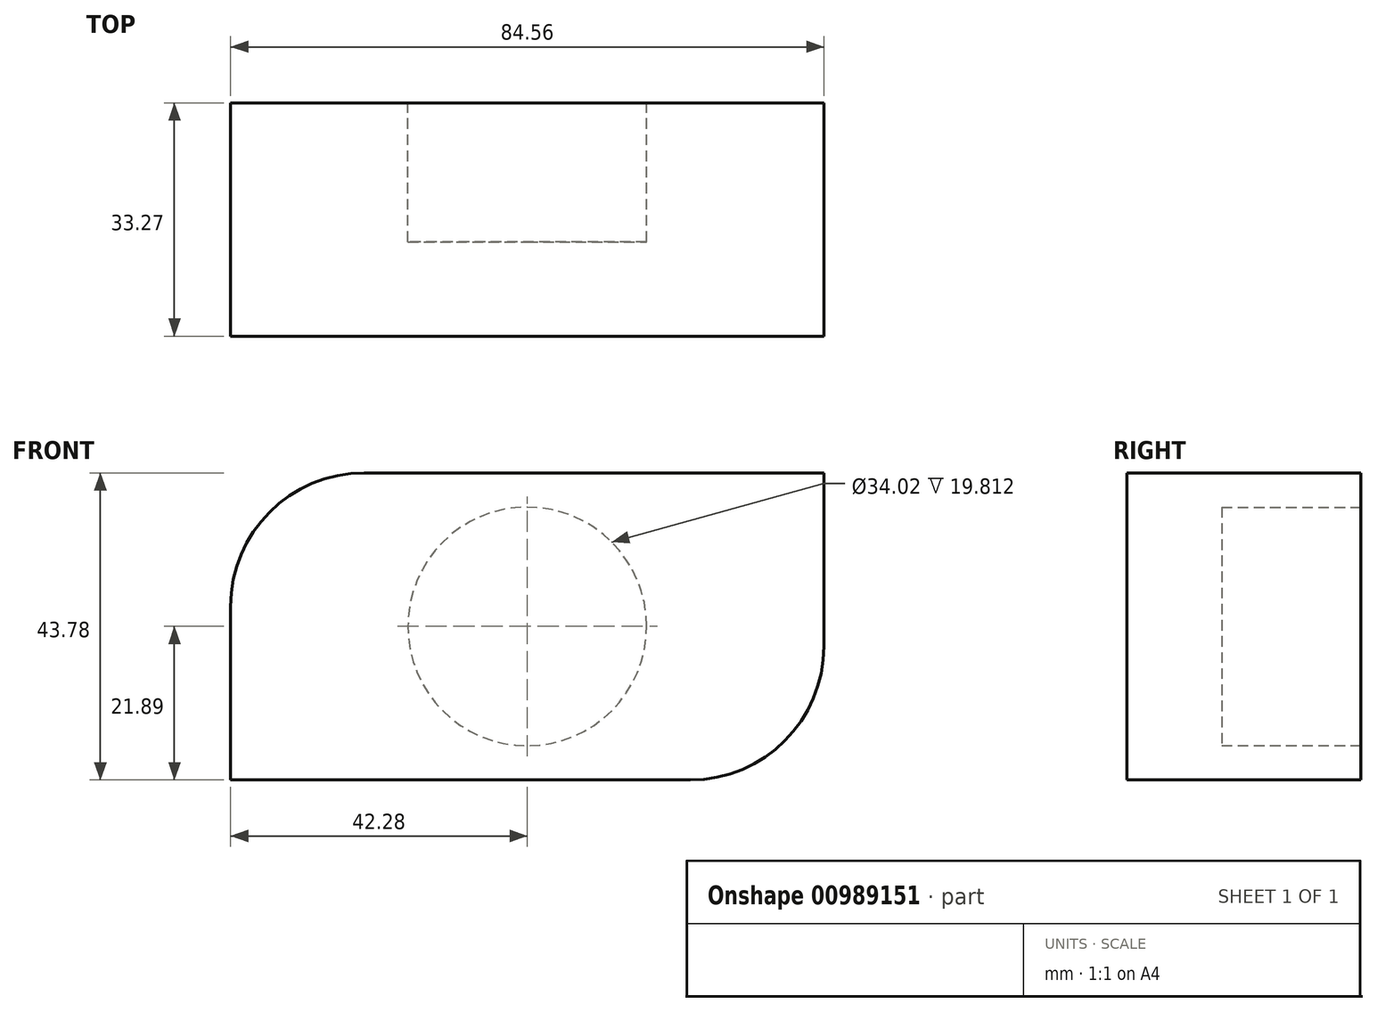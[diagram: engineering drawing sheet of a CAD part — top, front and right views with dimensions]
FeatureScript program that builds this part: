
annotation { "Feature Type Name" : "Feature", "Feature Type Description" : "" }
export const myFeature = defineFeature(function(context is Context, id is Id, definition is map)
    precondition{}
    {
        {
            var Q0;
            Q0=qCreatedBy(makeId("Front.planeOp"),FACE);
            var sketch = newSketch(context, id + "F0", { "sketchPlane" : qUnion([Q0])});
            skLineSegment(sketch, "E0.bottom", {"start": v(-42.28, -21.89) * mm, "end": v(23.23, -21.89) * mm});
            skLineSegment(sketch, "E0.top", {"start": v(-23.23, 21.89) * mm, "end": v(42.28, 21.89) * mm});
            skLineSegment(sketch, "E0.left", {"start": v(-42.28, -21.89) * mm, "end": v(-42.28, 2.84) * mm});
            skLineSegment(sketch, "E0.right", {"start": v(42.28, -2.84) * mm, "end": v(42.28, 21.89) * mm});
            skPoint(sketch, "E0.middle", {"position": v(0, 0) * mm});
            skPoint(sketch, "E1.visualSharp", {"position": v(-42.28, 21.89) * mm});
            skArc(sketch, "E1.filletArc", {"start": v(-23.23, 21.89) * mm, "mid": v(-36.7, 16.31) * mm, "end": v(-42.28, 2.84) * mm});
            skPoint(sketch, "E2.visualSharp", {"position": v(42.28, -21.89) * mm});
            skArc(sketch, "E2.filletArc", {"start": v(23.23, -21.89) * mm, "mid": v(36.7, -16.31) * mm, "end": v(42.28, -2.84) * mm});
            skSolve(sketch);
        }
        {
            var Q0;
            Q0 = qSketchRegion(id + "F0", true);
            extrude(context, id + "F1", {"entities" : qUnion([Q0]), "depth" : 33.27 * mm, "offsetDistance" : 25.4 * mm});
        }
        {
            var Q0;
            Q0=makeQuery(id+"F1.opExtrude","CAP_FACE",FACE,{"disambiguationData":[OSD([sQuery(id+"F0.wireOp",EDGE,"E0.bottom"),sQuery(id+"F0.wireOp",EDGE,"E0.top"),sQuery(id+"F0.wireOp",EDGE,"E0.left"),sQuery(id+"F0.wireOp",EDGE,"E0.right"),sQuery(id+"F0.wireOp",EDGE,"E1.filletArc"),sQuery(id+"F0.wireOp",EDGE,"E2.filletArc")])],"isStart":true});
            var sketch = newSketch(context, id + "F2", { "sketchPlane" : qUnion([Q0])});
            skCircle(sketch, "E3", {"center": v(0, 0) * mm, "radius": 17.01 * mm});
            skSolve(sketch);
        }
        {
            var Q0;
            Q0 = qSketchRegion(id + "F2", true);
            extrude(context, id + "F3", {"entities" : qUnion([Q0]), "operationType" : NewBodyOperationType.REMOVE, "oppositeDirection" : true, "depth" : 19.8 * mm, "offsetDistance" : 25.4 * mm});
        }
    });
